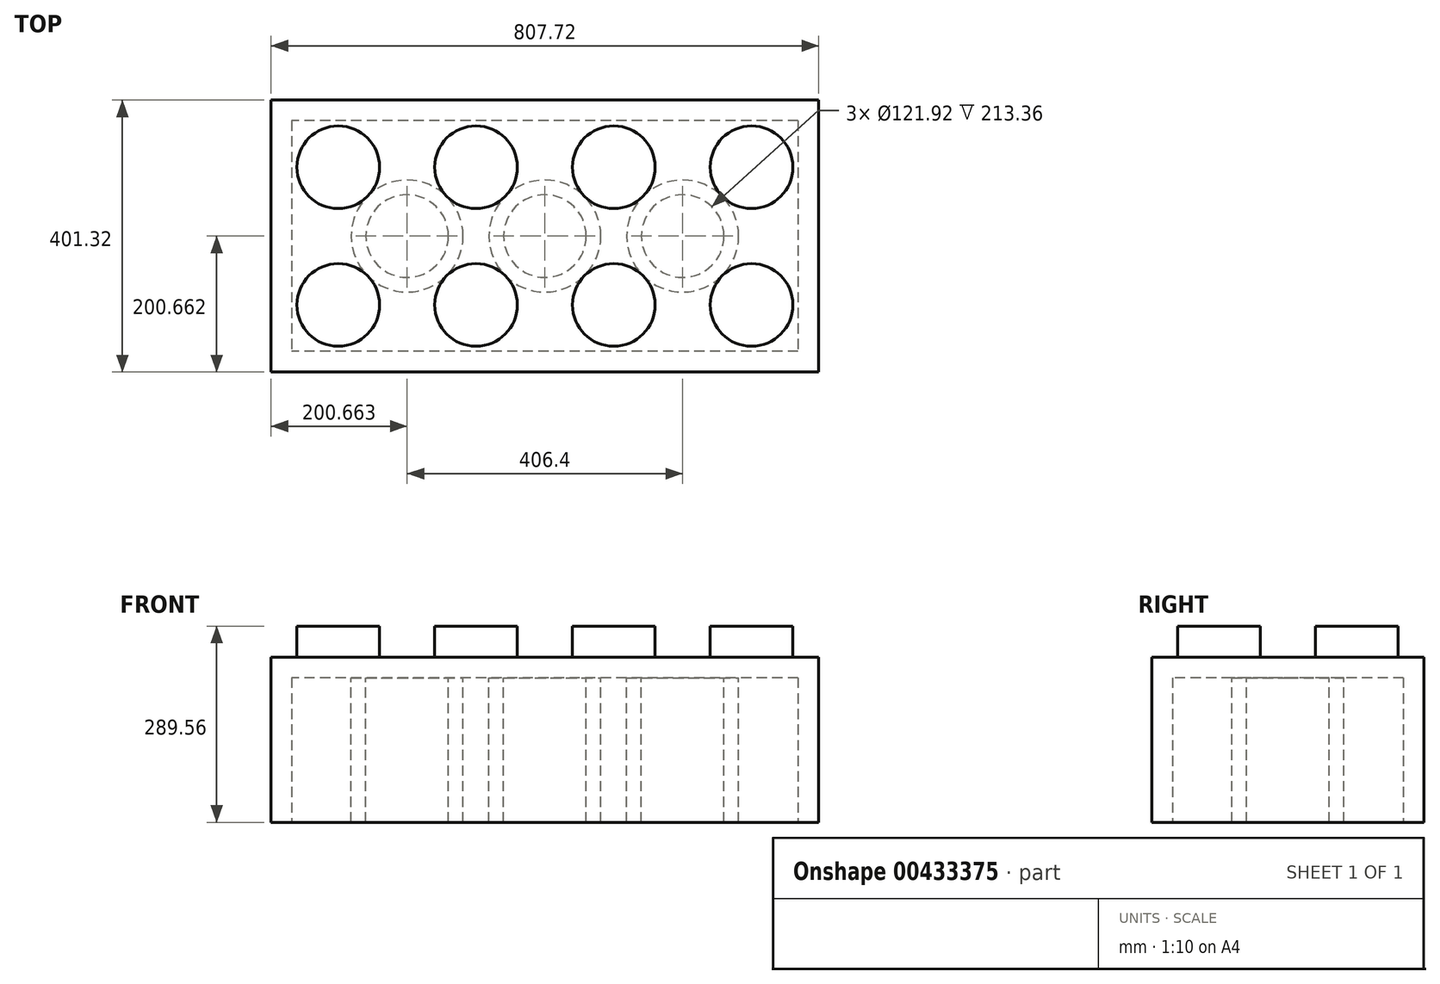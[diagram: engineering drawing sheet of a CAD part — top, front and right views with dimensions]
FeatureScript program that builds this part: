
annotation { "Feature Type Name" : "Feature", "Feature Type Description" : "" }
export const myFeature = defineFeature(function(context is Context, id is Id, definition is map)
    precondition{}
    {
        {
            var Q0;
            Q0=qCreatedBy(makeId("Top.planeOp"),FACE);
            var sketch = newSketch(context, id + "F0", { "sketchPlane" : qUnion([Q0])});
            skLineSegment(sketch, "E0.bottom", {"start": v(-407.55, 145.27) * mm, "end": v(400.17, 145.27) * mm});
            skLineSegment(sketch, "E0.top", {"start": v(-407.55, -256.05) * mm, "end": v(400.17, -256.05) * mm});
            skLineSegment(sketch, "E0.left", {"start": v(-407.55, 145.27) * mm, "end": v(-407.55, -256.05) * mm});
            skLineSegment(sketch, "E0.right", {"start": v(400.17, 145.27) * mm, "end": v(400.17, -256.05) * mm});
            skSolve(sketch);
        }
        {
            var Q0;
            Q0=makeQuery(id+"F0.imprint","IMPRINT",FACE,{"disambiguationData":[TD([[makeQuery(id+"F0.imprint","IMPRINT",EDGE,{"derivedFrom":sQuery(id+"F0.wireOp",EDGE,"E0.bottom")}),-1.0]])]});
            extrude(context, id + "F1", {"entities" : qUnion([Q0]), "depth" : 243.84 * mm});
        }
        {
            var Q0;
            Q0=makeQuery(id+"F1.opExtrude","CAP_FACE",FACE,{"disambiguationData":[OSD([sQuery(id+"F0.wireOp",EDGE,"E0.bottom"),sQuery(id+"F0.wireOp",EDGE,"E0.top"),sQuery(id+"F0.wireOp",EDGE,"E0.left"),sQuery(id+"F0.wireOp",EDGE,"E0.right")])],"isStart":false});
            var sketch = newSketch(context, id + "F2", { "sketchPlane" : qUnion([Q0])});
            skCircle(sketch, "E1", {"center": v(301.11, -156.99) * mm, "radius": 60.96 * mm});
            skCircle(sketch, "E2.0.1.0", {"center": v(301.11, 46.21) * mm, "radius": 60.96 * mm});
            skCircle(sketch, "E2.1.0.0", {"center": v(97.91, -156.99) * mm, "radius": 60.96 * mm});
            skCircle(sketch, "E2.1.1.0", {"center": v(97.91, 46.21) * mm, "radius": 60.96 * mm});
            skCircle(sketch, "E2.2.0.0", {"center": v(-105.29, -156.99) * mm, "radius": 60.96 * mm});
            skCircle(sketch, "E2.2.1.0", {"center": v(-105.29, 46.21) * mm, "radius": 60.96 * mm});
            skCircle(sketch, "E2.3.0.0", {"center": v(-308.49, -156.99) * mm, "radius": 60.96 * mm});
            skCircle(sketch, "E2.3.1.0", {"center": v(-308.49, 46.21) * mm, "radius": 60.96 * mm});
            skLineSegment(sketch, "E2.direction1", {"start": v(301.11, -156.99) * mm, "end": v(97.91, -156.99) * mm, "construction": true});
            skLineSegment(sketch, "E2.direction2", {"start": v(301.11, -156.99) * mm, "end": v(301.11, 46.21) * mm, "construction": true});
            skSolve(sketch);
        }
        {
            var Q0;
            Q0=makeQuery(id+"F2.imprint","IMPRINT",FACE,{"disambiguationData":[TD([[makeQuery(id+"F2.imprint","IMPRINT",EDGE,{"derivedFrom":sQuery(id+"F2.wireOp",EDGE,"E1")}),1.0]])]});
            var Q1;
            Q1=makeQuery(id+"F2.imprint","IMPRINT",FACE,{"disambiguationData":[TD([[makeQuery(id+"F2.imprint","IMPRINT",EDGE,{"derivedFrom":sQuery(id+"F2.wireOp",EDGE,"E2.0.1.0")}),1.0]])]});
            var Q2;
            Q2=makeQuery(id+"F2.imprint","IMPRINT",FACE,{"disambiguationData":[TD([[makeQuery(id+"F2.imprint","IMPRINT",EDGE,{"derivedFrom":sQuery(id+"F2.wireOp",EDGE,"E2.1.1.0")}),1.0]])]});
            var Q3;
            Q3=makeQuery(id+"F2.imprint","IMPRINT",FACE,{"disambiguationData":[TD([[makeQuery(id+"F2.imprint","IMPRINT",EDGE,{"derivedFrom":sQuery(id+"F2.wireOp",EDGE,"E2.1.0.0")}),1.0]])]});
            var Q4;
            Q4=makeQuery(id+"F2.imprint","IMPRINT",FACE,{"disambiguationData":[TD([[makeQuery(id+"F2.imprint","IMPRINT",EDGE,{"derivedFrom":sQuery(id+"F2.wireOp",EDGE,"E2.2.0.0")}),1.0]])]});
            var Q5;
            Q5=makeQuery(id+"F2.imprint","IMPRINT",FACE,{"disambiguationData":[TD([[makeQuery(id+"F2.imprint","IMPRINT",EDGE,{"derivedFrom":sQuery(id+"F2.wireOp",EDGE,"E2.2.1.0")}),1.0]])]});
            var Q6;
            Q6=makeQuery(id+"F2.imprint","IMPRINT",FACE,{"disambiguationData":[TD([[makeQuery(id+"F2.imprint","IMPRINT",EDGE,{"derivedFrom":sQuery(id+"F2.wireOp",EDGE,"E2.3.1.0")}),1.0]])]});
            var Q7;
            Q7=makeQuery(id+"F2.imprint","IMPRINT",FACE,{"disambiguationData":[TD([[makeQuery(id+"F2.imprint","IMPRINT",EDGE,{"derivedFrom":sQuery(id+"F2.wireOp",EDGE,"E2.3.0.0")}),1.0]])]});
            extrude(context, id + "F3", {"entities" : qUnion([Q0, Q1, Q2, Q3, Q4, Q5, Q6, Q7]), "operationType" : NewBodyOperationType.ADD, "depth" : 45.72 * mm});
        }
        {
            var Q0;
            Q0=makeQuery(id+"F1.opExtrude","CAP_FACE",FACE,{"disambiguationData":[OSD([sQuery(id+"F0.wireOp",EDGE,"E0.bottom"),sQuery(id+"F0.wireOp",EDGE,"E0.top"),sQuery(id+"F0.wireOp",EDGE,"E0.left"),sQuery(id+"F0.wireOp",EDGE,"E0.right")])],"isStart":true});
            var sketch = newSketch(context, id + "F4", { "sketchPlane" : qUnion([Q0])});
            skLineSegment(sketch, "E3.bottom", {"start": v(369.7, -114.8) * mm, "end": v(-377.07, -114.8) * mm});
            skLineSegment(sketch, "E3.top", {"start": v(369.7, 225.57) * mm, "end": v(-377.07, 225.57) * mm});
            skLineSegment(sketch, "E3.left", {"start": v(369.7, -114.8) * mm, "end": v(369.7, 225.57) * mm});
            skLineSegment(sketch, "E3.right", {"start": v(-377.07, -114.8) * mm, "end": v(-377.07, 225.57) * mm});
            skSolve(sketch);
        }
        {
            var Q0;
            Q0=makeQuery(id+"F4.imprint","IMPRINT",FACE,{"disambiguationData":[TD([[makeQuery(id+"F4.imprint","IMPRINT",EDGE,{"derivedFrom":sQuery(id+"F4.wireOp",EDGE,"E3.bottom")}),-1.0]])]});
            extrude(context, id + "F5", {"entities" : qUnion([Q0]), "operationType" : NewBodyOperationType.REMOVE, "oppositeDirection" : true, "depth" : 213.36 * mm});
        }
        {
            var Q0;
            Q0=makeQuery(id+"F5.boolean.opBoolean","COPY",FACE,{"derivedFrom":makeQuery(id+"F5.opExtrude","CAP_FACE",FACE,{"disambiguationData":[OSD([sQuery(id+"F4.wireOp",EDGE,"E3.bottom"),sQuery(id+"F4.wireOp",EDGE,"E3.top"),sQuery(id+"F4.wireOp",EDGE,"E3.left"),sQuery(id+"F4.wireOp",EDGE,"E3.right")])],"isStart":false})});
            var sketch = newSketch(context, id + "F6", { "sketchPlane" : qUnion([Q0])});
            skCircle(sketch, "E4", {"center": v(-3.69, 55.39) * mm, "radius": 82.55 * mm});
            skCircle(sketch, "E5", {"center": v(-3.69, 55.39) * mm, "radius": 60.96 * mm});
            skCircle(sketch, "E6.1.0.0", {"center": v(199.51, 55.39) * mm, "radius": 82.55 * mm});
            skCircle(sketch, "E6.1.0.1", {"center": v(199.51, 55.39) * mm, "radius": 60.96 * mm});
            skLineSegment(sketch, "E6.direction1", {"start": v(-3.69, 55.39) * mm, "end": v(199.51, 55.39) * mm, "construction": true});
            skCircle(sketch, "E7.1.0.0", {"center": v(-206.89, 55.39) * mm, "radius": 60.96 * mm});
            skCircle(sketch, "E7.1.0.1", {"center": v(-206.89, 55.39) * mm, "radius": 82.55 * mm});
            skLineSegment(sketch, "E7.direction1", {"start": v(-3.69, 55.39) * mm, "end": v(-206.89, 55.39) * mm, "construction": true});
            skSolve(sketch);
        }
        {
            var Q0;
            Q0=makeQuery(id+"F6.imprint","IMPRINT",FACE,{"disambiguationData":[TD([[makeQuery(id+"F6.imprint","IMPRINT",EDGE,{"derivedFrom":sQuery(id+"F6.wireOp",EDGE,"E7.1.0.0")}),-1.0]])]});
            var Q1;
            Q1=makeQuery(id+"F6.imprint","IMPRINT",FACE,{"disambiguationData":[TD([[makeQuery(id+"F6.imprint","IMPRINT",EDGE,{"derivedFrom":sQuery(id+"F6.wireOp",EDGE,"E4")}),1.0]])]});
            var Q2;
            Q2=makeQuery(id+"F6.imprint","IMPRINT",FACE,{"disambiguationData":[TD([[makeQuery(id+"F6.imprint","IMPRINT",EDGE,{"derivedFrom":sQuery(id+"F6.wireOp",EDGE,"E6.1.0.0")}),1.0]])]});
            extrude(context, id + "F7", {"entities" : qUnion([Q0, Q1, Q2]), "operationType" : NewBodyOperationType.ADD, "depth" : 213.36 * mm});
        }
    });
